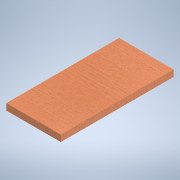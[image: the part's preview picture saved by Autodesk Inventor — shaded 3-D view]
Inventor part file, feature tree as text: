
AUTODESK INVENTOR PART (.ipt)
format: ipt  version: 2022 (Build 260153000, 153)  size: 105,984 bytes
history: native  units: in
note: dims shown in document units (in); Inventor stores cm internally (conversion verified against a paired STEP export)
features: extrude x1, sketch x1
ambient origin geometry x8: Origin, YZ Plane, XZ Plane, XY Plane, X Axis, Y Axis, Z Axis, Center Point
bodies: Solid1 (feature_tree)
feature tree (2):
  extrude  "Extrusion1"  Depth=15.0in
  sketch  "Sketch1"  dims[d0=7.25in d1=15.0in d2=0.852in d3=0.0in]
